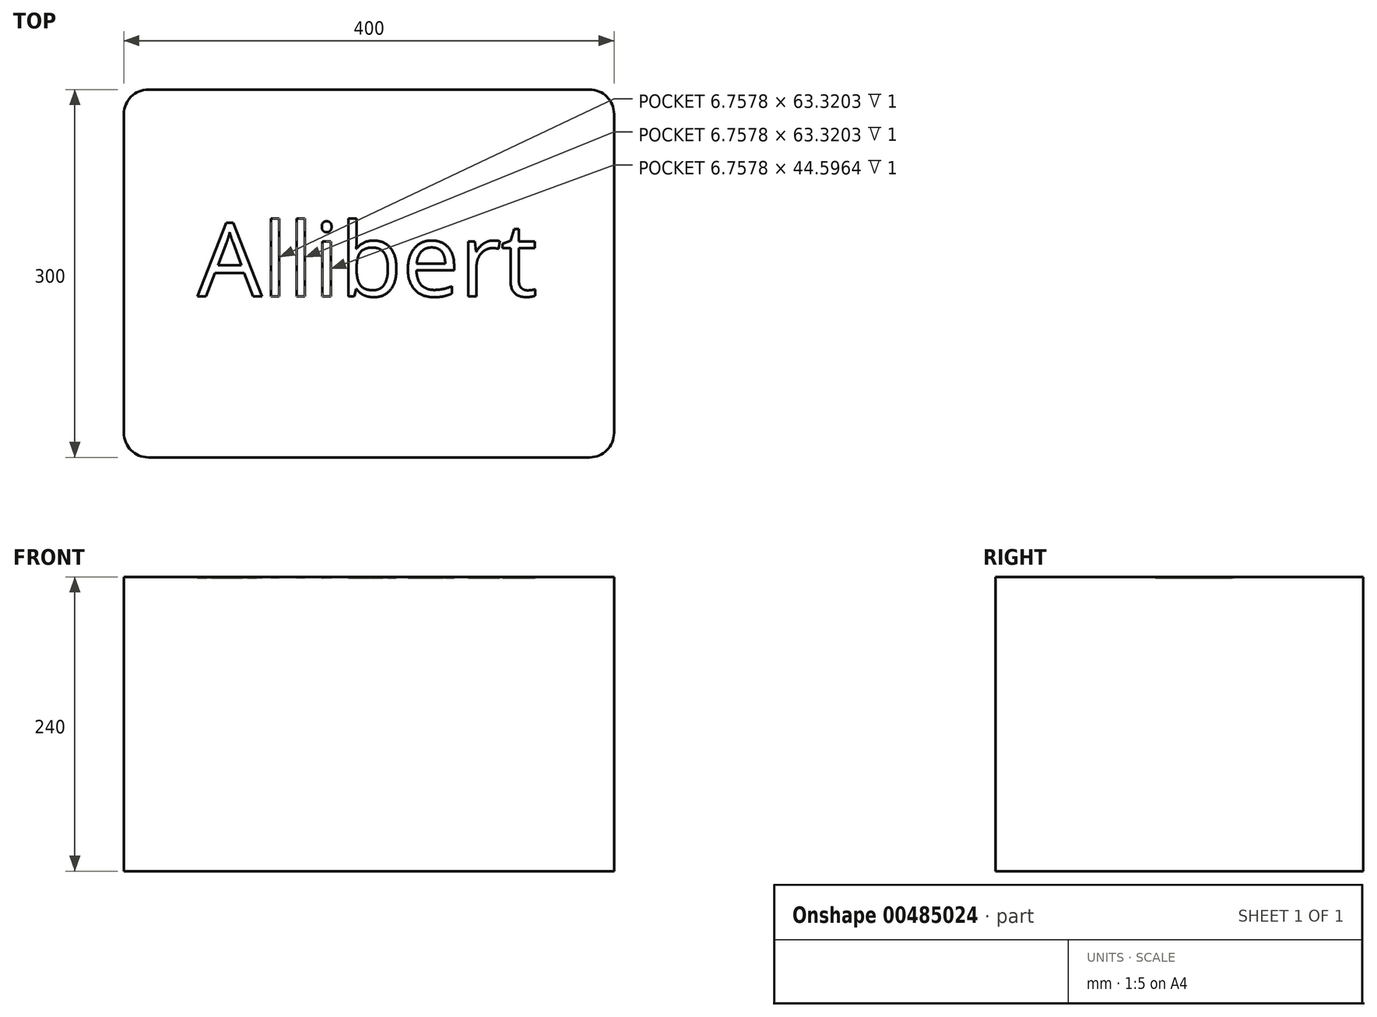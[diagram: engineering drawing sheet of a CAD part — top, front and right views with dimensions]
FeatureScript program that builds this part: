
annotation { "Feature Type Name" : "Feature", "Feature Type Description" : "" }
export const myFeature = defineFeature(function(context is Context, id is Id, definition is map)
    precondition{}
    {
        {
            var Q0;
            Q0=qCreatedBy(makeId("Top.planeOp"),FACE);
            var sketch = newSketch(context, id + "F0", { "sketchPlane" : qUnion([Q0])});
            skLineSegment(sketch, "E0.bottom", {"start": v(-200, 150) * mm, "end": v(200, 150) * mm});
            skLineSegment(sketch, "E0.top", {"start": v(-200, -150) * mm, "end": v(200, -150) * mm});
            skLineSegment(sketch, "E0.left", {"start": v(-200, 150) * mm, "end": v(-200, -150) * mm});
            skLineSegment(sketch, "E0.right", {"start": v(200, 150) * mm, "end": v(200, -150) * mm});
            skPoint(sketch, "E0.middle", {"position": v(0, 0) * mm});
            skSolve(sketch);
        }
        {
            var Q0;
            Q0 = qSketchRegion(id + "F0", true);
            extrude(context, id + "F1", {"entities" : qUnion([Q0]), "depth" : 240 * mm, "offsetDistance" : 25 * mm});
        }
        {
            var Q0;
            Q0=makeQuery(id+"F1.opExtrude","CAP_FACE",FACE,{"disambiguationData":[OSD([sQuery(id+"F0.wireOp",EDGE,"E0.bottom"),sQuery(id+"F0.wireOp",EDGE,"E0.top"),sQuery(id+"F0.wireOp",EDGE,"E0.left"),sQuery(id+"F0.wireOp",EDGE,"E0.right")])],"isStart":false});
            var sketch = newSketch(context, id + "F2", { "sketchPlane" : qUnion([Q0])});
            skText(sketch, "E1", { "text": "Allibert", "fontName": "OpenSans-Regular.ttf"});
            const initialGuessF2  = {"E1": [-0.14, -0.01854, 1, 0, 0.06]};
            skSetInitialGuess(sketch, initialGuessF2);
            skSolve(sketch);
        }
        {
            var Q0;
            Q0 = qSketchRegion(id + "F2", true);
            extrude(context, id + "F3", {"entities" : qUnion([Q0]), "operationType" : NewBodyOperationType.REMOVE, "oppositeDirection" : true, "depth" : 1 * mm, "offsetDistance" : 25 * mm});
        }
        {
            var Q0;
            Q0=makeQuery(id+"F1.opExtrude","SWEPT_EDGE",EDGE,{"disambiguationData":[OSD([sQuery(id+"F0.wireOp",EDGE,"E0.top"),sQuery(id+"F0.wireOp",EDGE,"E0.left")])]});
            var Q1;
            Q1=makeQuery(id+"F1.opExtrude","SWEPT_EDGE",EDGE,{"disambiguationData":[OSD([sQuery(id+"F0.wireOp",EDGE,"E0.bottom"),sQuery(id+"F0.wireOp",EDGE,"E0.left")])]});
            var Q2;
            Q2=makeQuery(id+"F1.opExtrude","SWEPT_EDGE",EDGE,{"disambiguationData":[OSD([sQuery(id+"F0.wireOp",EDGE,"E0.top"),sQuery(id+"F0.wireOp",EDGE,"E0.right")])]});
            var Q3;
            Q3=makeQuery(id+"F1.opExtrude","SWEPT_EDGE",EDGE,{"disambiguationData":[OSD([sQuery(id+"F0.wireOp",EDGE,"E0.bottom"),sQuery(id+"F0.wireOp",EDGE,"E0.right")])]});
            fillet(context, id + "F4", {"entities" : qUnion([Q0, Q1, Q2, Q3]), "radius" : 20 * mm, "tangentPropagation" : true, "allowEdgeOverflow" : false});
        }
    });
